# Revit family: Gleitlager T ohne Schalldämmung, Ø64 bis Ø219mm
name_source: partatom
category: HLS-Bauteile
revit_build: Autodesk Revit 2018 (Build: 20190510_1515(x64)
units: mm (PartAtom-declared; Revit-internal decimal feet)

## family parameters
Arbeitsebenenbasiert = Ja
Beim Laden mit Abzugskörper schneiden = Nein
Bemaßung runder Anschluss = Durchmesser verwenden
Gemeinsam genutzt = Ja
Immer vertikal = Nein
Klassifizierung = Keine
Raumberechnungspunkt = Nein
Teiletyp = Normal

## types (13) — shared parameters
Breite Schellenband = 50 mm
Breite Unterbau = 100 mm
Fabrikat = MEFA
Höhe Unterbau = 105 mm
Kurztext1 = Gleitlager T h=105 50 x 5 mm
Länge Unterbau = 250 mm
Mengeneinheit = St
Schalldämmeinlage = ohne Dämmung
Sicherheitsfaktor = 1.54
Verschluss-Schraube = M12
Vorgabe-Ansicht = 1219 mm
vpe = 1
zero-valued in all types: Dämmstärke, Stärke, max. Rohraußendurchmesser, min. Rohraußendurchmesser

## per-type parameters (varying)
| type | Artikelnummer | EAN | Gewicht | Gewicht pro Bauteil | Hersteller | Kurztext2 | RS Titan Ø64 bis Ø219 |
| Gleitlager T Ø 108, o.Däm. | 145fa0108 | 4250928459930 | 6.74 kg | 6.74 kg |  | 108 mm o. Dämm. fsv | Rohrschelle Titan HD, o.A, o.D, 30Grad : Titan HD, o.A., Ø108mm |
| Gleitlager T Ø  89, o.Däm. | 145fa0089 | 4250928459923 | 6.48 kg | 6.48 kg |  | 89 mm o. Dämm. fsv | Rohrschelle Titan HD, o.A, o.D, 30Grad : Titan HD, o.A., Ø89mm |
| Gleitlager T Ø  76, o.Däm. | 145fa0076 | 4250928459916 | 6.29 kg | 6.29 kg | MEFA | 76 mm o. Dämm. fsv | Rohrschelle Titan HD, o.A, o.D, 30Grad : Titan HD, o.A., Ø76mm |
| Gleitlager T Ø  64, o.Däm. | 145fa0064 | 4250928459909 | 6.13 kg | 6.13 kg | MEFA | 64 mm o. Dämm. fsv | Rohrschelle Titan HD, o.A, o.D, 30Grad : Titan HD, o.A., Ø64mm |
| Gleitlager T Ø 110, o.Däm. | 145fa0110 | 4250928459947 | 6.77 kg | 6.77 kg |  | 110 mm o. Dämm. fsv | Rohrschelle Titan HD, o.A, o.D, 30Grad : Titan HD, o.A., Ø110mm |
| Gleitlager T Ø 114, o.Däm. | 145fa0114 | 4250928459954 | 6.83 kg | 6.83 kg |  | 114 mm o. Dämm. fsv | Rohrschelle Titan HD, o.A, o.D, 30Grad : Titan HD, o.A., Ø114mm |
| Gleitlager T Ø 133, o.Däm. | 145fa0133 | 4250928459961 | 7.09 kg | 7.09 kg |  | 133 mm o. Dämm. fsv | Rohrschelle Titan HD, o.A, o.D, 30Grad : Titan HD, o.A., Ø133mm |
| Gleitlager T Ø 140, o.Däm. | 145fa0140 | 4250928459978 | 7.19 kg | 7.19 kg |  | 140 mm o. Dämm. fsv | Rohrschelle Titan HD, o.A, o.D, 30Grad : Titan HD, o.A., Ø140mm |
| Gleitlager T Ø 160, o.Däm. | 145fa0160 | 4250928459985 | 7.47 kg | 7.47 kg |  | 160 mm o. Dämm. fsv | Rohrschelle Titan HD, o.A, o.D, 30Grad : Titan HD, o.A., Ø160mm |
| Gleitlager T Ø 168, o.Däm. | 145fa0168 | 4250928459992 | 7.58 kg | 7.58 kg |  | 168 mm o. Dämm. fsv | Rohrschelle Titan HD, o.A, o.D, 30Grad : Titan HD, o.A., Ø168mm |
| Gleitlager T Ø 180, o.Däm. | 145fa0180 | 4250928460004 | 7.74 kg | 7.74 kg |  | 180 mm o. Dämm. fsv | Rohrschelle Titan HD, o.A, o.D, 30Grad : Titan HD, o.A., Ø180mm |
| Gleitlager T Ø 210, o.Däm. | 145fa0210 | 4250928460011 | 8.16 kg | 8.16 kg |  | 210 mm o. Dämm. fsv | Rohrschelle Titan HD, o.A, o.D, 30Grad : Titan HD, o.A., Ø210mm |
| Gleitlager T Ø 219, o.Däm. | 145fa0219 | 4250928460028 | 8.29 kg | 8.29 kg |  | 219 mm o. Dämm. fsv | Rohrschelle Titan HD, o.A, o.D, 30Grad : Titan HD, o.A., Ø219mm |

## geometry (parser evidence)
native form markers: Sweep x8
no freeform markers — native parametric forms only
